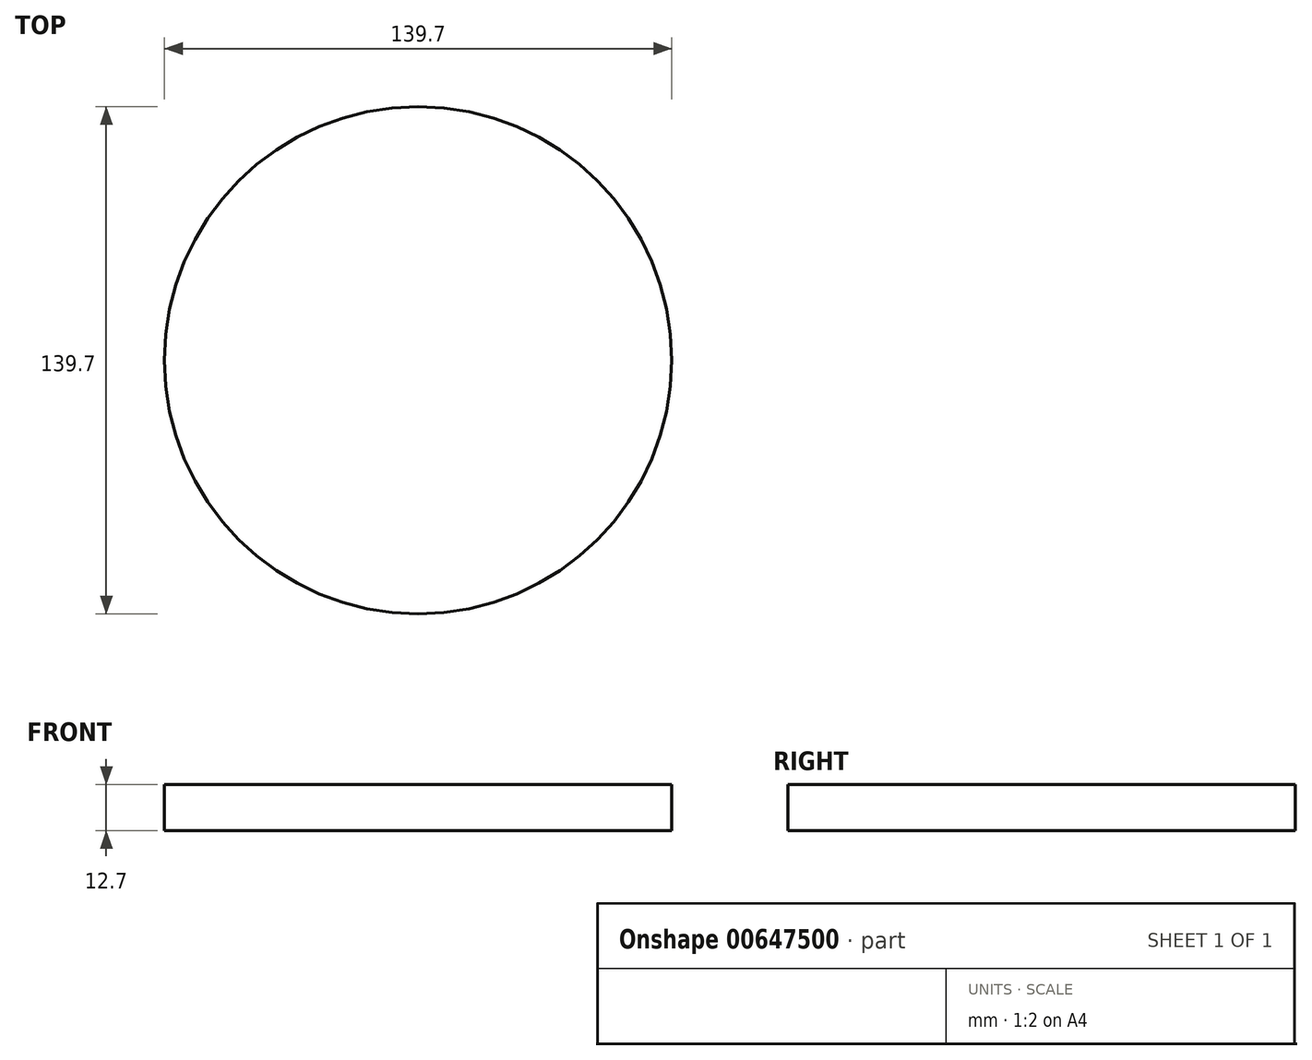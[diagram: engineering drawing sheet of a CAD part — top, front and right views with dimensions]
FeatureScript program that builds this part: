
annotation { "Feature Type Name" : "Feature", "Feature Type Description" : "" }
export const myFeature = defineFeature(function(context is Context, id is Id, definition is map)
    precondition{}
    {
        {
            var Q0;
            Q0=qCreatedBy(makeId("Top.planeOp"),FACE);
            var sketch = newSketch(context, id + "F0", { "sketchPlane" : qUnion([Q0])});
            skCircle(sketch, "E0", {"center": v(0, 0) * mm, "radius": 69.85 * mm});
            skSolve(sketch);
        }
        {
            var Q0;
            Q0=qSketchRegion(id+"F0",true);
            extrude(context, id + "F1", {"entities" : qUnion([Q0]), "depth" : 12.7 * mm});
        }
    });
